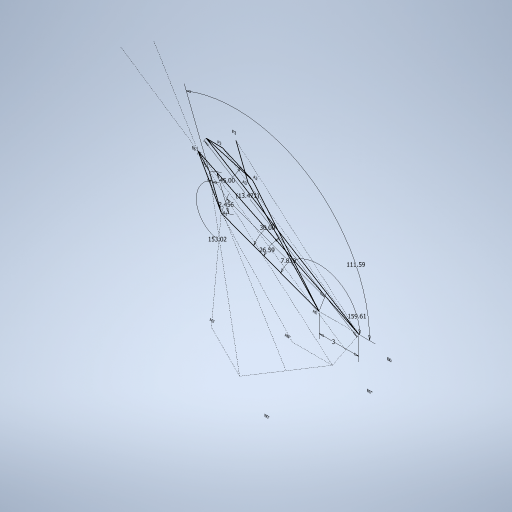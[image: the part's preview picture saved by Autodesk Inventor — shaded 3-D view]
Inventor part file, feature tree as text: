
AUTODESK INVENTOR PART (.ipt)
format: ipt  version: 2024 (Build 280153000, 153)  size: 266,240 bytes
history: native  units: in
note: dims shown in document units (in); Inventor stores cm internally (conversion verified against a paired STEP export)
features: sketch x1
ambient origin geometry x8: Origin, YZ Plane, XZ Plane, XY Plane, X Axis, Y Axis, Z Axis, Center Point
feature tree (1):
  sketch  "Sketch1"  dims[d0=0.3086in d1=0.0967in d2=1.0967in d3=0.7667in d4=30.0deg d5=45.0deg d6=0.1827in d7=1.0515in d9=0.1181in d10=0.5304in]
